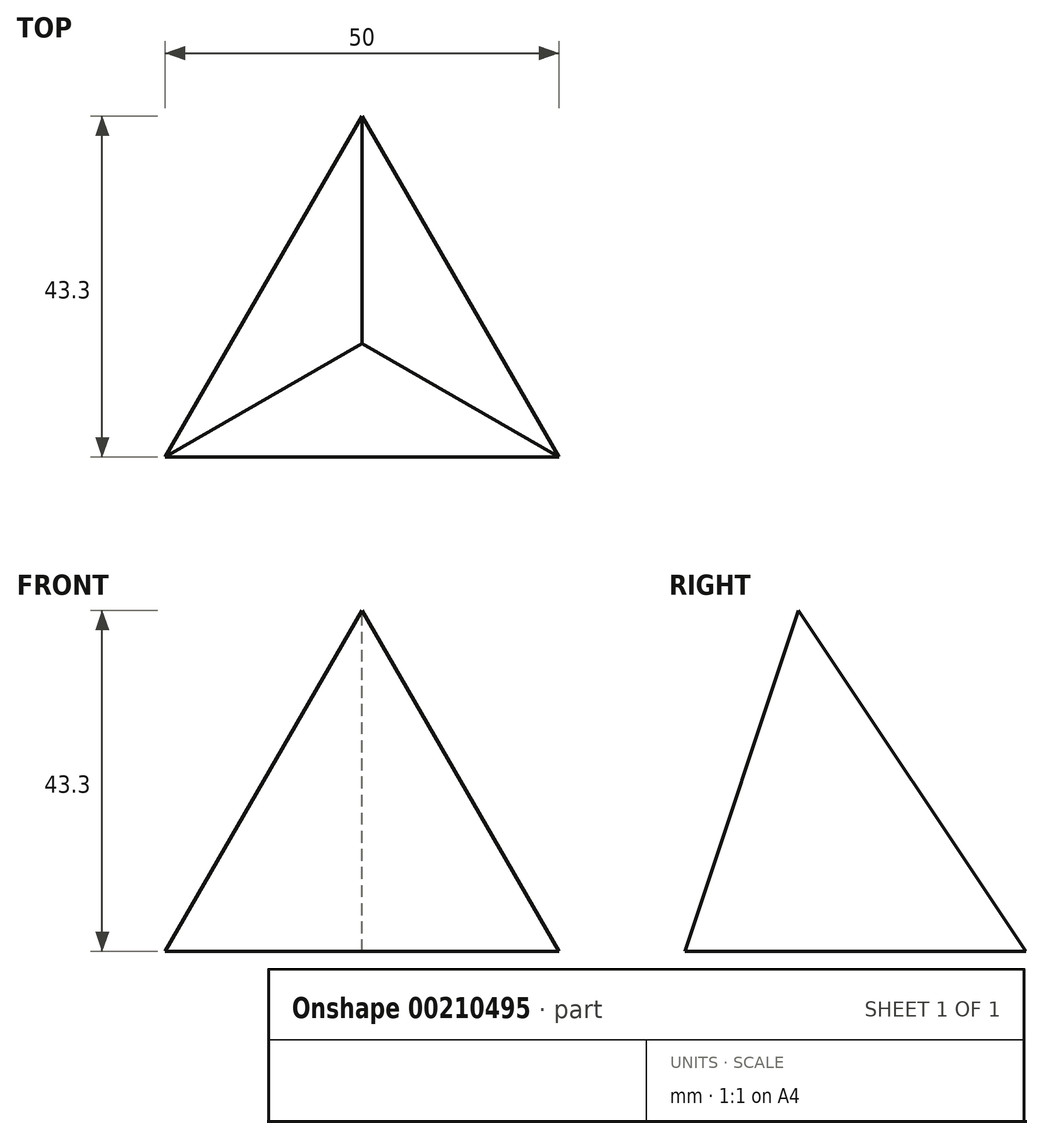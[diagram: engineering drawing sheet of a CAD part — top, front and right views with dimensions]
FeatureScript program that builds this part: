
annotation { "Feature Type Name" : "Feature", "Feature Type Description" : "" }
export const myFeature = defineFeature(function(context is Context, id is Id, definition is map)
    precondition{}
    {
        {
            var Q0;
            Q0=qCreatedBy(makeId("Top.planeOp"),FACE);
            var sketch = newSketch(context, id + "F0", { "sketchPlane" : qUnion([Q0])});
            skCircle(sketch, "E0.cCircle", {"center": v(0, 0) * mm, "radius": 14.43 * mm, "construction": true});
            skLineSegment(sketch, "E0.0", {"start": v(-25, -14.43) * mm, "end": v(0, 28.87) * mm});
            skLineSegment(sketch, "E0.1", {"start": v(0, 28.87) * mm, "end": v(25, -14.43) * mm});
            skLineSegment(sketch, "E0.2", {"start": v(25, -14.43) * mm, "end": v(-25, -14.43) * mm});
            skPoint(sketch, "E0.0.midPoint", {"position": v(-12.5, 7.22) * mm});
            skSolve(sketch);
        }
        {
            var Q0;
            Q0=qCreatedBy(makeId("Front.planeOp"),FACE);
            var sketch = newSketch(context, id + "F1", { "sketchPlane" : qUnion([Q0])});
            skPoint(sketch, "E1", {"position": v(0, 43.3) * mm});
            skSolve(sketch);
        }
        {
            var Q0;
            Q0=qSketchRegion(id+"F0",true);
            var Q1;
            Q1=sQuery(id+"F1.wireOp",VERTEX,"E1");
            loft(context, id + "F2", {"sheetProfilesArray" : [{ "sheetProfileEntities" : qUnion([Q0]) }, { "sheetProfileEntities" : qUnion([Q1]) }]});
        }
    });
